# Revit family: DC_Holyoake_MEQ_RLL-25_13
name_source: partatom
category: Air Terminals
revit_build: Autodesk Revit 2013 (Build: 20120221_2030(x64)
units: mm (PartAtom-declared; Revit-internal decimal feet)

## types (1)
- DC_Holyoake_MEQ_RLL-25_13
    Act Louver Number = 6
    Blade Length = 158 mm
    Calc Length = 175 mm  [stored 0.574147 ft]
    Calc Width = 100 mm  [stored 0.328084 ft]
    Depth = 32 mm  [stored 0.104987 ft]
    Holyoake Product Range = Holyoake Exhaust and Return Grilles
    Length = 175 mm  [stored 0.574147 ft]
    Manufacturer = Holyoake
    Material-Body = Holyoake White
    Max Flow = 2400.0 L/s
    Min Flow = 20.0 L/s
    Model = Holyoake RLL-25
    Noise Level NC Max = 60
    Noise Level NC Min = 10
    Static Pressure Max = 93.0 Pa
    Static Pressure Min = 5.0 Pa
    Type Comments = RLL Exhaust and Return Grilles
    URL = www.holyoake.com.au
    Width = 100 mm  [stored 0.328084 ft]

note: [stored X ft] marks values corroborated as IEEE doubles in the binary element streams (Revit-internal decimal feet)

## geometry (parser evidence)
native form markers: Blend x2, Sweep x20
no freeform markers — native parametric forms only
